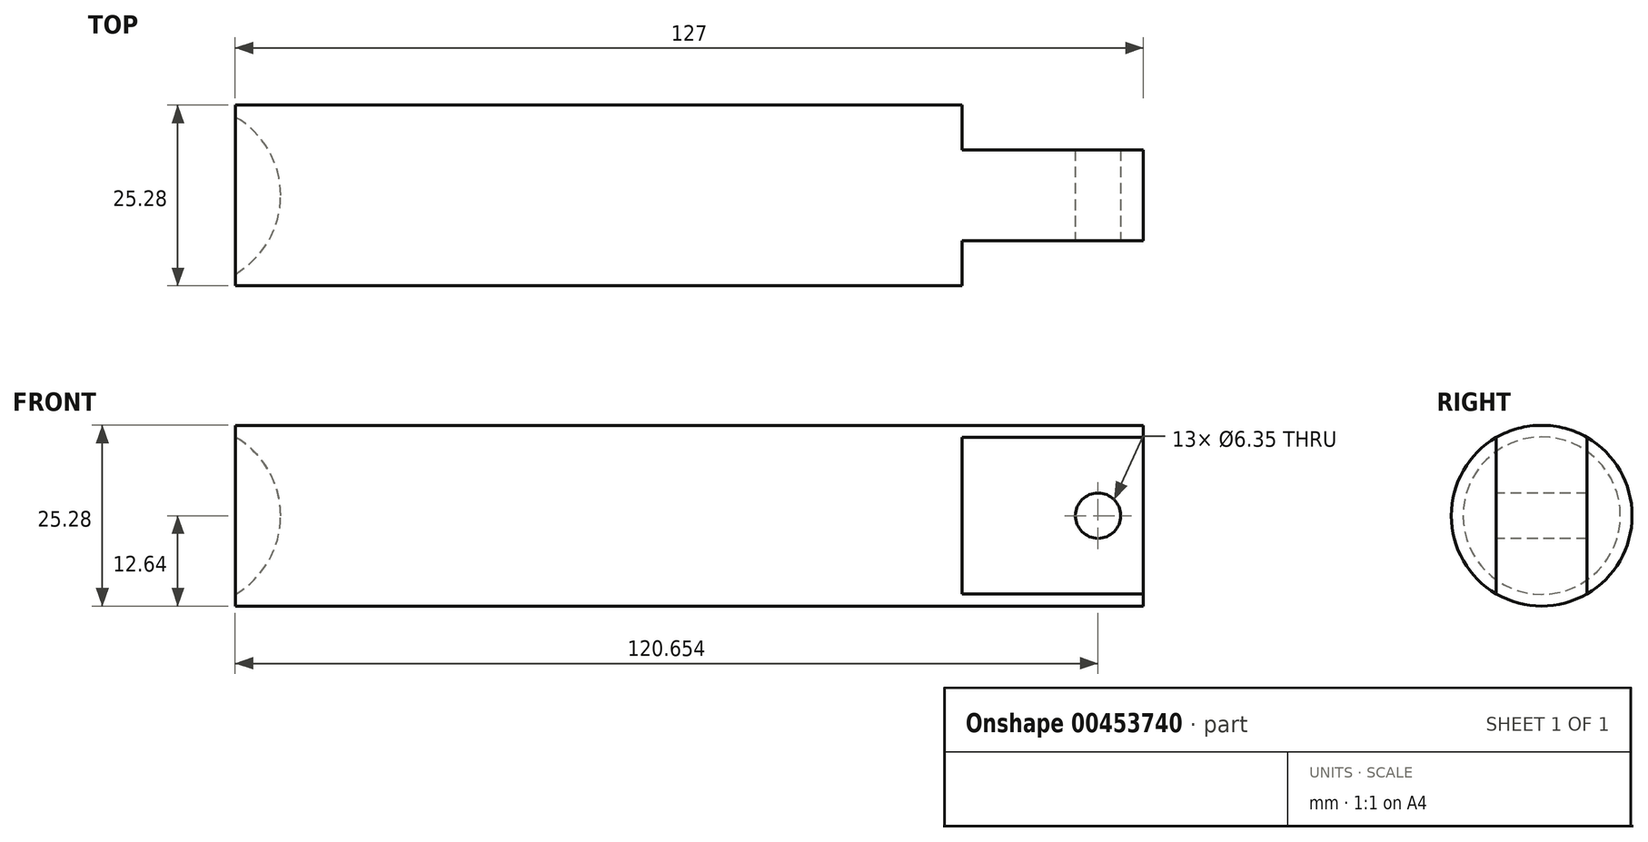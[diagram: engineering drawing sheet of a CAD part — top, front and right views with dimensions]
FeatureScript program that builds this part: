
annotation { "Feature Type Name" : "Feature", "Feature Type Description" : "" }
export const myFeature = defineFeature(function(context is Context, id is Id, definition is map)
    precondition{}
    {
        {
            var Q0;
            Q0=qCreatedBy(makeId("Front.planeOp"),FACE);
            var sketch = newSketch(context, id + "F0", { "sketchPlane" : qUnion([Q0])});
            skLineSegment(sketch, "E0", {"start": v(-54.47, 11) * mm, "end": v(-54.47, 12.64) * mm});
            skLineSegment(sketch, "E1", {"start": v(-54.47, 12.64) * mm, "end": v(72.53, 12.64) * mm});
            skLineSegment(sketch, "E2", {"start": v(72.53, 12.64) * mm, "end": v(72.53, 0) * mm});
            skLineSegment(sketch, "E3", {"start": v(72.53, 0) * mm, "end": v(-48.12, 0) * mm});
            skLineSegment(sketch, "E4", {"start": v(-60.82, 17.68) * mm, "end": v(-60.82, -20.03) * mm});
            skArc(sketch, "E5", {"start": v(-48.12, 0) * mm, "mid": v(-49.82, 6.35) * mm, "end": v(-54.47, 11) * mm});
            skPoint(sketch, "E6.orphan", {"position": v(-54.47, 0) * mm});
            skLineSegment(sketch, "E7", {"start": v(-73.27, 0) * mm, "end": v(109.3, 0) * mm});
            skSolve(sketch);
        }
        {
            var Q0;
            Q0=makeQuery(id+"F0.imprint","IMPRINT",FACE,{"disambiguationData":[TD([[makeQuery(id+"F0.imprint","IMPRINT",EDGE,{"derivedFrom":sQuery(id+"F0.wireOp",EDGE,"E0")}),-1.0]])]});
            var Q1;
            Q1=sQuery(id+"F0.wireOp",EDGE,"E7");
            revolve(context, id + "F1", {"entities" : qUnion([Q0]), "axis" : qUnion([Q1]), "revolveType" : RevolveType.FULL});
        }
        {
            var Q0;
            Q0=makeQuery(id+"F1.opRevolve","SWEPT_FACE",FACE,{"disambiguationData":[OSD([sQuery(id+"F0.wireOp",EDGE,"E2")])]});
            var sketch = newSketch(context, id + "F2", { "sketchPlane" : qUnion([Q0])});
            skLineSegment(sketch, "E8", {"start": v(-6.35, 10.93) * mm, "end": v(-6.35, -10.93) * mm});
            skLineSegment(sketch, "E9", {"start": v(6.35, 10.93) * mm, "end": v(6.35, -10.93) * mm});
            skArc(sketch, "E10", {"start": v(-6.35, 10.93) * mm, "mid": v(-12.64, 0) * mm, "end": v(-6.35, -10.93) * mm});
            skArc(sketch, "E11.trimOffspring", {"start": v(6.35, -10.93) * mm, "mid": v(12.64, 0) * mm, "end": v(6.35, 10.93) * mm});
            skSolve(sketch);
        }
        {
            var Q0;
            Q0=makeQuery(id+"F2.imprint","IMPRINT",FACE,{"disambiguationData":[TD([[makeQuery(id+"F2.imprint","IMPRINT",EDGE,{"derivedFrom":sQuery(id+"F2.wireOp",EDGE,"E8")}),-1.0]])]});
            var Q1;
            Q1=makeQuery(id+"F2.imprint","IMPRINT",FACE,{"disambiguationData":[TD([[makeQuery(id+"F2.imprint","IMPRINT",EDGE,{"derivedFrom":sQuery(id+"F2.wireOp",EDGE,"E9")}),1.0]])]});
            extrude(context, id + "F3", {"entities" : qUnion([Q0, Q1]), "operationType" : NewBodyOperationType.REMOVE, "oppositeDirection" : true, "depth" : 25.4 * mm});
        }
        {
            var Q0;
            Q0=makeQuery(id+"F3.boolean.opBoolean","COPY",FACE,{"derivedFrom":makeQuery(id+"F3.opExtrude","SWEPT_FACE",FACE,{"disambiguationData":[OSD([sQuery(id+"F2.wireOp",EDGE,"E8")])]})});
            var sketch = newSketch(context, id + "F4", { "sketchPlane" : qUnion([Q0])});
            skCircle(sketch, "E12", {"center": v(66.18, 0) * mm, "radius": 3.18 * mm});
            skSolve(sketch);
        }
        {
            var Q0;
            Q0=makeQuery(id+"F4.imprint","IMPRINT",FACE,{"disambiguationData":[TD([[makeQuery(id+"F4.imprint","IMPRINT",EDGE,{"derivedFrom":sQuery(id+"F4.wireOp",EDGE,"E12")}),1.0]])]});
            extrude(context, id + "F5", {"entities" : qUnion([Q0]), "operationType" : NewBodyOperationType.REMOVE, "endBound" : BoundingType.THROUGH_ALL, "oppositeDirection" : true, "depth" : 25.4 * mm});
        }
    });
